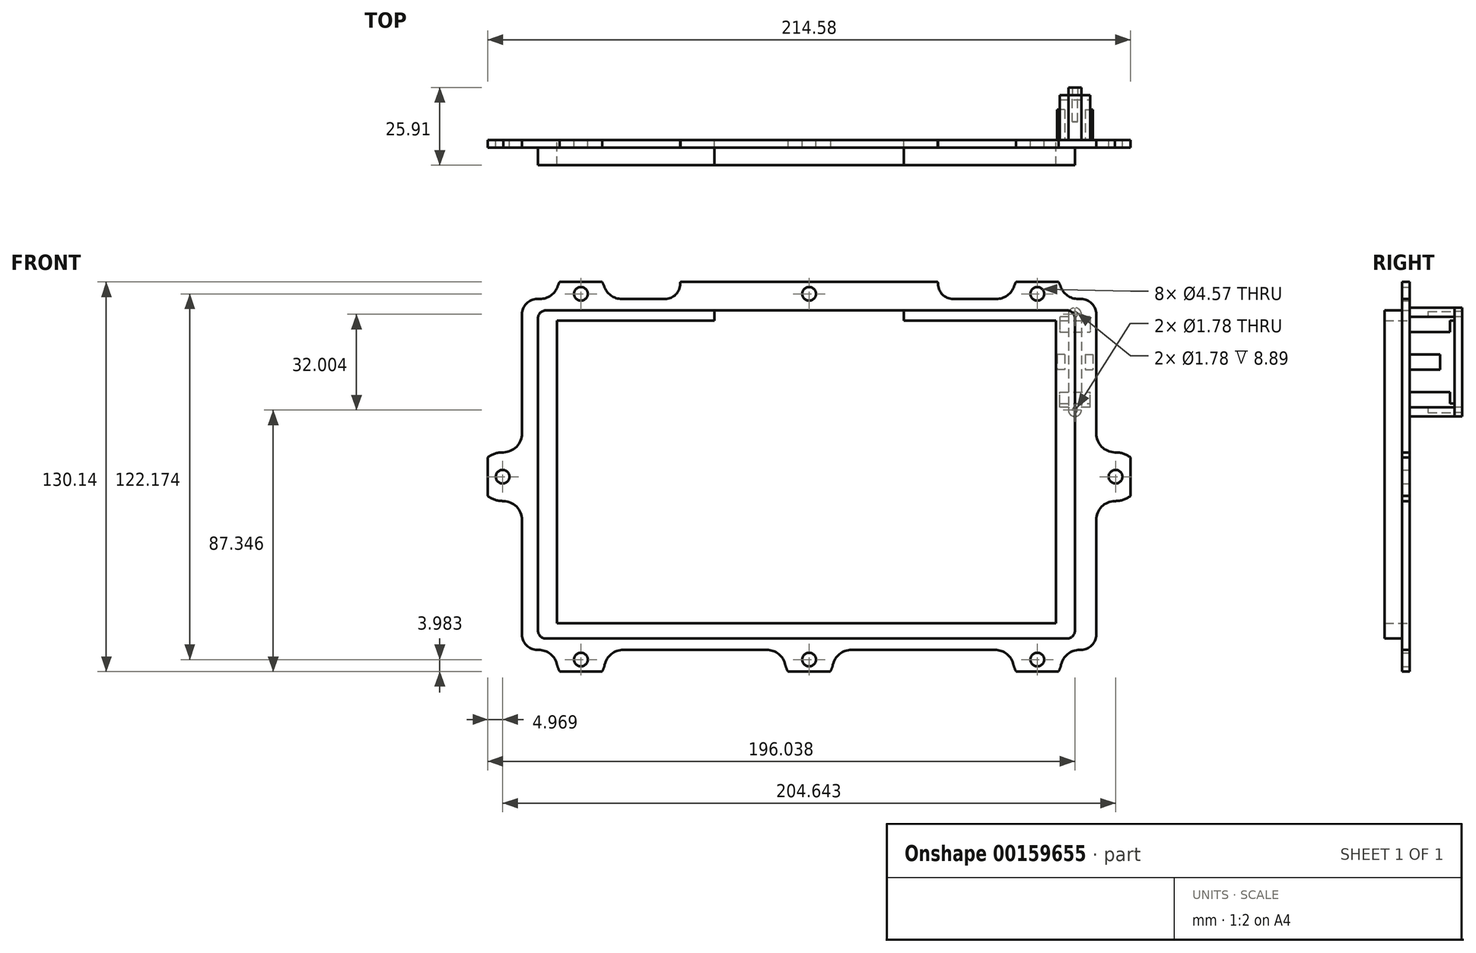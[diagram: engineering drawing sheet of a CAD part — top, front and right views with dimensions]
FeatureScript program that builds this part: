
annotation { "Feature Type Name" : "Feature", "Feature Type Description" : "" }
export const myFeature = defineFeature(function(context is Context, id is Id, definition is map)
    precondition{}
    {
        {
            var Q0;
            Q0=qCreatedBy(makeId("Front.planeOp"),FACE);
            var sketch = newSketch(context, id + "F0", { "sketchPlane" : qUnion([Q0])});
            skLineSegment(sketch, "E0.bottom", {"start": v(122.56, 76.2) * mm, "end": v(-122.56, 76.2) * mm});
            skLineSegment(sketch, "E0.top", {"start": v(122.55, -76.2) * mm, "end": v(-122.55, -76.2) * mm});
            skLineSegment(sketch, "E0.left", {"start": v(122.55, 76.2) * mm, "end": v(122.56, -76.2) * mm});
            skLineSegment(sketch, "E0.right", {"start": v(-122.56, 76.2) * mm, "end": v(-122.55, -76.2) * mm});
            skPoint(sketch, "E0.middle", {"position": v(0, 0) * mm});
            skLineSegment(sketch, "E1.bottom", {"start": v(-84.15, -48.95) * mm, "end": v(82.4, -48.95) * mm});
            skLineSegment(sketch, "E1.top", {"start": v(-84.15, 52.12) * mm, "end": v(-31.6, 52.12) * mm});
            skLineSegment(sketch, "E1.left", {"start": v(-84.15, -48.95) * mm, "end": v(-84.15, 52.12) * mm});
            skLineSegment(sketch, "E1.right", {"start": v(82.4, -48.95) * mm, "end": v(82.4, 52.12) * mm});
            skLineSegment(sketch, "E2", {"start": v(0, 76.2) * mm, "end": v(0, -76.2) * mm, "construction": true});
            skCircle(sketch, "E3", {"center": v(0, -61.09) * mm, "radius": 2.29 * mm});
            skCircle(sketch, "E4.MirrorC", {"center": v(0, 61.09) * mm, "radius": 2.29 * mm});
            skLineSegment(sketch, "E5.top", {"start": v(31.6, 55.55) * mm, "end": v(-31.6, 55.55) * mm});
            skLineSegment(sketch, "E5.left", {"start": v(31.6, 55.55) * mm, "end": v(31.6, 52.12) * mm});
            skLineSegment(sketch, "E5.right", {"start": v(-31.6, 55.55) * mm, "end": v(-31.6, 52.12) * mm});
            skLineSegment(sketch, "E6.trimOffspring", {"start": v(31.6, 52.12) * mm, "end": v(82.4, 52.12) * mm});
            skPoint(sketch, "E7.centerSnap0", {"position": v(-84.15, 1.59) * mm});
            skCircle(sketch, "E8", {"center": v(-102.32, 0) * mm, "radius": 2.29 * mm});
            skPoint(sketch, "E8.centerSnap0", {"position": v(-122.55, 0) * mm});
            skCircle(sketch, "E9.MirrorC", {"center": v(102.32, 0) * mm, "radius": 2.29 * mm});
            skCircle(sketch, "E10", {"center": v(-76.2, 61.09) * mm, "radius": 2.29 * mm});
            skCircle(sketch, "E11.MirrorC", {"center": v(76.2, 61.09) * mm, "radius": 2.29 * mm});
            skCircle(sketch, "E12.MirrorC", {"center": v(-76.2, -61.09) * mm, "radius": 2.29 * mm});
            skCircle(sketch, "E13.MirrorC", {"center": v(76.2, -61.09) * mm, "radius": 2.29 * mm});
            skSolve(sketch);
        }
        {
            var Q0;
            Q0 = qSketchRegion(id + "F0", true);
            extrude(context, id + "F1", {"entities" : qUnion([Q0]), "depth" : 2.54 * mm});
        }
        {
            var Q0;
            {var subQ0=sQuery(id+"F0.wireOp",EDGE,"E6.trimOffspring");var subQ1=sQuery(id+"F0.wireOp",EDGE,"E5.left");var subQ2=sQuery(id+"F0.wireOp",EDGE,"E1.bottom");var subQ3=sQuery(id+"F0.wireOp",EDGE,"E5.right");var subQ4=sQuery(id+"F0.wireOp",EDGE,"E0.right");var subQ5=sQuery(id+"F0.wireOp",EDGE,"E0.left");var subQ6=sQuery(id+"F0.wireOp",EDGE,"E0.bottom");var subQ7=sQuery(id+"F0.wireOp",EDGE,"E1.top");var subQ8=sQuery(id+"F0.wireOp",EDGE,"E1.left");var subQ9=sQuery(id+"F0.wireOp",EDGE,"E5.top");var subQ10=sQuery(id+"F0.wireOp",EDGE,"E1.right");Q0=makeQuery(id+"FoEDC6IaHk2UjBE_1.boolean.opBoolean","SPLIT",FACE,{"disambiguationData":[TD([makeQuery(id+"F1.opExtrude","SWEPT_FACE",FACE,{"disambiguationData":[OSD([subQ6])]})])],"derivedFrom":makeQuery(id+"F1.opExtrude","CAP_FACE",FACE,{"disambiguationData":[OSD([subQ6,sQuery(id+"F0.wireOp",EDGE,"E0.top"),subQ5,subQ4,subQ2,subQ7,subQ8,subQ10,sQuery(id+"F0.wireOp",EDGE,"E3"),sQuery(id+"F0.wireOp",EDGE,"sFVqbhVj-slte-m2BO-i9PR-RLCebhDjpQio"),sQuery(id+"F0.wireOp",EDGE,"nxVHSm6B-fOxF-N3zU-KlmY-iFDlvtlfsas0"),sQuery(id+"F0.wireOp",EDGE,"0cddea9b-7ac9-488d-9e64-17cf55ce85570.MirrorC"),sQuery(id+"F0.wireOp",EDGE,"E4.MirrorC"),sQuery(id+"F0.wireOp",EDGE,"3127313a-c26d-4710-95f3-0c9ef9dcd8090.MirrorC"),subQ9,subQ1,subQ3,subQ0])],"isStart":false})});}
            var sketch = newSketch(context, id + "F2", { "sketchPlane" : qUnion([Q0])});
            skLineSegment(sketch, "E14.bottom", {"start": v(88.75, -54.03) * mm, "end": v(-90.5, -54.03) * mm});
            skLineSegment(sketch, "E14.top", {"start": v(88.75, 55.55) * mm, "end": v(31.6, 55.55) * mm});
            skLineSegment(sketch, "E14.left", {"start": v(88.75, -54.03) * mm, "end": v(88.75, 55.55) * mm});
            skLineSegment(sketch, "E14.right", {"start": v(-90.5, -54.03) * mm, "end": v(-90.5, 55.55) * mm});
            skLineSegment(sketch, "E15.bottom", {"start": v(-84.15, -48.95) * mm, "end": v(82.4, -48.95) * mm});
            skLineSegment(sketch, "E15.top", {"start": v(-84.15, 52.12) * mm, "end": v(-31.6, 52.12) * mm});
            skLineSegment(sketch, "E15.left", {"start": v(-84.15, -48.95) * mm, "end": v(-84.15, 52.12) * mm});
            skLineSegment(sketch, "E15.right", {"start": v(82.4, -48.95) * mm, "end": v(82.4, 52.12) * mm});
            skLineSegment(sketch, "E16", {"start": v(31.6, 52.12) * mm, "end": v(31.6, 55.55) * mm});
            skLineSegment(sketch, "E17", {"start": v(-31.6, 52.12) * mm, "end": v(-31.6, 55.55) * mm});
            skLineSegment(sketch, "E18.trimOffspring", {"start": v(-31.6, 55.55) * mm, "end": v(-90.5, 55.55) * mm});
            skLineSegment(sketch, "E19.trimOffspring", {"start": v(31.6, 52.12) * mm, "end": v(82.4, 52.12) * mm});
            skSolve(sketch);
        }
        {
            var Q0;
            Q0 = qSketchRegion(id + "F2", true);
            extrude(context, id + "F3", {"entities" : qUnion([Q0]), "operationType" : NewBodyOperationType.ADD, "depth" : 5.84 * mm});
        }
        {
            var Q0;
            Q0=makeQuery(id+"F1.opExtrude","CAP_FACE",FACE,{"disambiguationData":[OSD([sQuery(id+"F0.wireOp",EDGE,"E0.bottom"),sQuery(id+"F0.wireOp",EDGE,"E0.top"),sQuery(id+"F0.wireOp",EDGE,"E0.left"),sQuery(id+"F0.wireOp",EDGE,"E0.right"),sQuery(id+"F0.wireOp",EDGE,"E1.bottom"),sQuery(id+"F0.wireOp",EDGE,"E1.top"),sQuery(id+"F0.wireOp",EDGE,"E1.left"),sQuery(id+"F0.wireOp",EDGE,"E1.right"),sQuery(id+"F0.wireOp",EDGE,"E3"),sQuery(id+"F0.wireOp",EDGE,"sFVqbhVj-slte-m2BO-i9PR-RLCebhDjpQio"),sQuery(id+"F0.wireOp",EDGE,"nxVHSm6B-fOxF-N3zU-KlmY-iFDlvtlfsas0"),sQuery(id+"F0.wireOp",EDGE,"0cddea9b-7ac9-488d-9e64-17cf55ce85570.MirrorC"),sQuery(id+"F0.wireOp",EDGE,"E4.MirrorC"),sQuery(id+"F0.wireOp",EDGE,"3127313a-c26d-4710-95f3-0c9ef9dcd8090.MirrorC"),sQuery(id+"F0.wireOp",EDGE,"E5.top"),sQuery(id+"F0.wireOp",EDGE,"E5.left"),sQuery(id+"F0.wireOp",EDGE,"E5.right"),sQuery(id+"F0.wireOp",EDGE,"E6.trimOffspring"),sQuery(id+"F0.wireOp",EDGE,"E8"),sQuery(id+"F0.wireOp",EDGE,"E9.MirrorC")])],"isStart":false});
            var sketch = newSketch(context, id + "F4", { "sketchPlane" : qUnion([Q0])});
            skLineSegment(sketch, "E20.bottom", {"start": v(-90.78, 59.36) * mm, "end": v(-89.92, 59.36) * mm});
            skLineSegment(sketch, "E20.top", {"start": v(-90.78, -57.84) * mm, "end": v(-90.34, -57.84) * mm});
            skLineSegment(sketch, "E20.left", {"start": v(-95.86, 54.28) * mm, "end": v(-95.86, 14.48) * mm});
            skLineSegment(sketch, "E20.right", {"start": v(95.86, 54.28) * mm, "end": v(95.86, 14.48) * mm});
            skArc(sketch, "E21.MirrorC", {"start": v(7.94, -62.83) * mm, "mid": v(0, -69.21) * mm, "end": v(-7.94, -62.83) * mm});
            skArc(sketch, "E22.0", {"start": v(-102.32, 8.13) * mm, "mid": v(-110.45, 0) * mm, "end": v(-102.32, -8.13) * mm});
            skArc(sketch, "E23.MirrorC", {"start": v(102.32, 8.13) * mm, "mid": v(110.45, 0) * mm, "end": v(102.32, -8.13) * mm});
            skLineSegment(sketch, "E24", {"start": v(-102.32, 8.13) * mm, "end": v(-102.14, 8.13) * mm});
            skLineSegment(sketch, "E25", {"start": v(-102.32, -8.13) * mm, "end": v(-102.14, -8.13) * mm});
            skLineSegment(sketch, "E26.MirrorCS", {"start": v(102.32, 8.13) * mm, "end": v(102.14, 8.13) * mm});
            skLineSegment(sketch, "E27.MirrorCS", {"start": v(102.32, -8.13) * mm, "end": v(102.14, -8.13) * mm});
            skLineSegment(sketch, "E28.trimOffspring", {"start": v(-62.48, 59.36) * mm, "end": v(-48.1, 59.36) * mm});
            skLineSegment(sketch, "E29.trimOffspring", {"start": v(48.1, 59.36) * mm, "end": v(62.48, 59.36) * mm});
            skLineSegment(sketch, "E30.trimOffspring", {"start": v(89.92, 59.36) * mm, "end": v(90.78, 59.36) * mm});
            skLineSegment(sketch, "E31.trimOffspring", {"start": v(95.86, -14.48) * mm, "end": v(95.86, -52.76) * mm});
            skLineSegment(sketch, "E32.trimOffspring", {"start": v(90.34, -57.84) * mm, "end": v(90.78, -57.84) * mm});
            skLineSegment(sketch, "E33.trimOffspring", {"start": v(14.14, -57.84) * mm, "end": v(62.06, -57.84) * mm});
            skLineSegment(sketch, "E34.trimOffspring", {"start": v(-62.06, -57.84) * mm, "end": v(-14.14, -57.84) * mm});
            skLineSegment(sketch, "E35.trimOffspring", {"start": v(-95.86, -14.48) * mm, "end": v(-95.86, -52.76) * mm});
            skLineSegment(sketch, "E36.bottom", {"start": v(-122.56, 76.2) * mm, "end": v(122.56, 76.2) * mm});
            skLineSegment(sketch, "E36.top", {"start": v(-122.56, -76.2) * mm, "end": v(122.56, -76.2) * mm});
            skLineSegment(sketch, "E36.left", {"start": v(-122.56, 76.2) * mm, "end": v(-122.56, -76.2) * mm});
            skLineSegment(sketch, "E36.right", {"start": v(122.56, 76.2) * mm, "end": v(122.56, -76.2) * mm});
            skLineSegment(sketch, "E37", {"start": v(43.03, 64.44) * mm, "end": v(43.03, 64.44) * mm});
            skLineSegment(sketch, "E38", {"start": v(40.49, 66.98) * mm, "end": v(8.65, 66.98) * mm});
            skLineSegment(sketch, "E39", {"start": v(-43.03, 64.44) * mm, "end": v(-43.03, 64.44) * mm});
            skPoint(sketch, "E40.MirrorCS.end.orphan", {"position": v(6.92, 59.36) * mm});
            skPoint(sketch, "E41.orphan", {"position": v(8.13, 61.09) * mm});
            skPoint(sketch, "E42.orphan", {"position": v(-6.92, 59.36) * mm});
            skPoint(sketch, "E43.orphan", {"position": v(-8.13, 61.09) * mm});
            skPoint(sketch, "E44.visualSharp", {"position": v(43.03, 59.36) * mm});
            skArc(sketch, "E44.filletArc", {"start": v(43.03, 64.44) * mm, "mid": v(44.52, 60.85) * mm, "end": v(48.1, 59.36) * mm});
            skPoint(sketch, "E45.visualSharp", {"position": v(-43.03, 59.36) * mm});
            skArc(sketch, "E45.filletArc", {"start": v(-48.1, 59.36) * mm, "mid": v(-44.52, 60.85) * mm, "end": v(-43.03, 64.44) * mm});
            skPoint(sketch, "E46.visualSharp", {"position": v(95.86, 59.36) * mm});
            skArc(sketch, "E46.filletArc", {"start": v(95.86, 54.28) * mm, "mid": v(94.37, 57.87) * mm, "end": v(90.78, 59.36) * mm});
            skPoint(sketch, "E47.visualSharp", {"position": v(95.86, -57.84) * mm});
            skArc(sketch, "E47.filletArc", {"start": v(90.78, -57.84) * mm, "mid": v(94.37, -56.35) * mm, "end": v(95.86, -52.76) * mm});
            skPoint(sketch, "E48.visualSharp", {"position": v(-95.86, -57.84) * mm});
            skArc(sketch, "E48.filletArc", {"start": v(-95.86, -52.76) * mm, "mid": v(-94.37, -56.35) * mm, "end": v(-90.78, -57.84) * mm});
            skPoint(sketch, "E49.visualSharp", {"position": v(-95.86, 59.36) * mm});
            skArc(sketch, "E49.filletArc", {"start": v(-90.78, 59.36) * mm, "mid": v(-94.37, 57.87) * mm, "end": v(-95.86, 54.28) * mm});
            skLineSegment(sketch, "E50.trimOffspring", {"start": v(8.65, 66.98) * mm, "end": v(-40.49, 66.98) * mm});
            skPoint(sketch, "E51.orphan", {"position": v(-6.92, -59.36) * mm});
            skPoint(sketch, "E52.orphan", {"position": v(6.92, -59.36) * mm});
            skPoint(sketch, "E53.orphan", {"position": v(-83.25, 59.36) * mm});
            skPoint(sketch, "E54.orphan", {"position": v(83.25, 59.36) * mm});
            skArc(sketch, "E55.0", {"start": v(-68.5, 63.68) * mm, "mid": v(-76.2, 69.22) * mm, "end": v(-83.9, 63.68) * mm});
            skArc(sketch, "E56.MirrorC", {"start": v(-68.26, -62.83) * mm, "mid": v(-76.2, -69.22) * mm, "end": v(-84.14, -62.83) * mm});
            skArc(sketch, "E57.MirrorC", {"start": v(68.26, -62.83) * mm, "mid": v(76.2, -69.22) * mm, "end": v(84.14, -62.83) * mm});
            skArc(sketch, "E58.MirrorC", {"start": v(68.5, 63.68) * mm, "mid": v(76.2, 69.22) * mm, "end": v(83.9, 63.68) * mm});
            skPoint(sketch, "E59.visualSharp", {"position": v(-43.03, 66.98) * mm});
            skArc(sketch, "E59.filletArc", {"start": v(-40.49, 66.98) * mm, "mid": v(-42.28, 66.24) * mm, "end": v(-43.03, 64.44) * mm});
            skPoint(sketch, "E60.visualSharp", {"position": v(43.03, 66.98) * mm});
            skArc(sketch, "E60.filletArc", {"start": v(43.03, 64.44) * mm, "mid": v(42.28, 66.24) * mm, "end": v(40.49, 66.98) * mm});
            skPoint(sketch, "E61.newPointA", {"position": v(-83.12, 59.86) * mm});
            skPoint(sketch, "E62.newPointA", {"position": v(-69.15, 59.36) * mm});
            skPoint(sketch, "E62.newPointB", {"position": v(-69.28, 59.86) * mm});
            skPoint(sketch, "E63.visualSharp", {"position": v(-95.86, 8.13) * mm});
            skPoint(sketch, "E64.visualSharp", {"position": v(-95.86, -8.13) * mm});
            skPoint(sketch, "E65.newPointB", {"position": v(-83.12, -59.86) * mm});
            skPoint(sketch, "E66.newPointA", {"position": v(-69.28, -59.86) * mm});
            skPoint(sketch, "E67.visualSharp", {"position": v(-6.92, -57.84) * mm});
            skPoint(sketch, "E68.visualSharp", {"position": v(6.92, -57.84) * mm});
            skPoint(sketch, "E69.newPointA", {"position": v(69.28, -59.86) * mm});
            skPoint(sketch, "E70.newPointA", {"position": v(83.12, -59.86) * mm});
            skPoint(sketch, "E71.visualSharp", {"position": v(95.86, -8.13) * mm});
            skPoint(sketch, "E72.visualSharp", {"position": v(95.86, 8.13) * mm});
            skPoint(sketch, "E73.newPointA", {"position": v(83.12, 59.86) * mm});
            skPoint(sketch, "E74.newPointA", {"position": v(69.28, 59.86) * mm});
            skPoint(sketch, "E74.newPointB", {"position": v(69.15, 59.36) * mm});
            skArc(sketch, "E75", {"start": v(-68.5, 63.68) * mm, "mid": v(-66.18, 60.55) * mm, "end": v(-62.48, 59.36) * mm});
            skArc(sketch, "E76", {"start": v(-89.92, 59.36) * mm, "mid": v(-86.22, 60.55) * mm, "end": v(-83.9, 63.68) * mm});
            skArc(sketch, "E77", {"start": v(-102.28, 8.13) * mm, "mid": v(-97.75, 9.96) * mm, "end": v(-95.86, 14.48) * mm});
            skArc(sketch, "E78", {"start": v(-7.94, -62.83) * mm, "mid": v(-10.16, -59.24) * mm, "end": v(-14.14, -57.84) * mm});
            skArc(sketch, "E79", {"start": v(-95.86, -14.48) * mm, "mid": v(-97.75, -9.96) * mm, "end": v(-102.28, -8.13) * mm});
            skArc(sketch, "E80", {"start": v(-84.14, -62.83) * mm, "mid": v(-86.36, -59.24) * mm, "end": v(-90.34, -57.84) * mm});
            skArc(sketch, "E81", {"start": v(-62.06, -57.84) * mm, "mid": v(-66.04, -59.24) * mm, "end": v(-68.26, -62.83) * mm});
            skArc(sketch, "E82", {"start": v(14.14, -57.84) * mm, "mid": v(10.16, -59.24) * mm, "end": v(7.94, -62.83) * mm});
            skArc(sketch, "E83", {"start": v(68.26, -62.83) * mm, "mid": v(66.04, -59.24) * mm, "end": v(62.06, -57.84) * mm});
            skArc(sketch, "E84", {"start": v(90.34, -57.84) * mm, "mid": v(86.36, -59.24) * mm, "end": v(84.14, -62.83) * mm});
            skArc(sketch, "E85", {"start": v(102.28, -8.13) * mm, "mid": v(97.75, -9.96) * mm, "end": v(95.86, -14.48) * mm});
            skArc(sketch, "E86", {"start": v(95.86, 14.48) * mm, "mid": v(97.75, 9.96) * mm, "end": v(102.28, 8.13) * mm});
            skArc(sketch, "E87", {"start": v(62.48, 59.36) * mm, "mid": v(66.18, 60.55) * mm, "end": v(68.5, 63.68) * mm});
            skArc(sketch, "E88", {"start": v(83.9, 63.68) * mm, "mid": v(86.22, 60.55) * mm, "end": v(89.92, 59.36) * mm});
            skPoint(sketch, "E89.start.orphan", {"position": v(-84.33, 61.09) * mm});
            skPoint(sketch, "E90.start.orphan", {"position": v(-68.07, 61.09) * mm});
            skPoint(sketch, "E91.orphan", {"position": v(-84.33, -61.09) * mm});
            skPoint(sketch, "E92.MirrorCS.start.orphan", {"position": v(-68.07, -61.09) * mm});
            skPoint(sketch, "E93.orphan", {"position": v(-8.13, -61.09) * mm});
            skPoint(sketch, "E94.orphan", {"position": v(8.13, -61.09) * mm});
            skPoint(sketch, "E95.orphan", {"position": v(68.07, -61.09) * mm});
            skPoint(sketch, "E96.orphan", {"position": v(84.33, -61.09) * mm});
            skPoint(sketch, "E97.MirrorCS.start.orphan", {"position": v(84.33, 61.09) * mm});
            skPoint(sketch, "E98.MirrorCS.start.orphan", {"position": v(68.07, 61.09) * mm});
            skSolve(sketch);
        }
        {
            var Q0;
            Q0 = qSketchRegion(id + "F4", true);
            extrude(context, id + "F5", {"entities" : qUnion([Q0]), "operationType" : NewBodyOperationType.REMOVE, "oppositeDirection" : true, "depth" : 25.4 * mm});
        }
        {
            var Q0;
            Q0=makeQuery(id+"F3.opExtrude","SWEPT_EDGE",EDGE,{"disambiguationData":[OSD([sQuery(id+"F2.wireOp",EDGE,"E14.right"),sQuery(id+"F2.wireOp",EDGE,"E18.trimOffspring")])]});
            var Q1;
            Q1=makeQuery(id+"F3.opExtrude","SWEPT_EDGE",EDGE,{"disambiguationData":[OSD([sQuery(id+"F2.wireOp",EDGE,"E14.bottom"),sQuery(id+"F2.wireOp",EDGE,"E14.right")])]});
            var Q2;
            Q2=makeQuery(id+"F3.opExtrude","SWEPT_EDGE",EDGE,{"disambiguationData":[OSD([sQuery(id+"F2.wireOp",EDGE,"E14.top"),sQuery(id+"F2.wireOp",EDGE,"E14.left")])]});
            var Q3;
            Q3=makeQuery(id+"F3.opExtrude","SWEPT_EDGE",EDGE,{"disambiguationData":[OSD([sQuery(id+"F2.wireOp",EDGE,"E14.bottom"),sQuery(id+"F2.wireOp",EDGE,"E14.left")])]});
            fillet(context, id + "F6", {"entities" : qUnion([Q0, Q1, Q2, Q3]), "radius" : 2.54 * mm, "tangentPropagation" : true, "allowEdgeOverflow" : false});
        }
        {
            var Q0;
            Q0=qCreatedBy(makeId("Front.planeOp"),FACE);
            var sketch = newSketch(context, id + "F7", { "sketchPlane" : qUnion([Q0])});
            skLineSegment(sketch, "E99.bottom", {"start": v(107.29, 65.07) * mm, "end": v(-107.29, 65.07) * mm});
            skLineSegment(sketch, "E99.top", {"start": v(107.29, -65.07) * mm, "end": v(-107.29, -65.07) * mm});
            skLineSegment(sketch, "E99.left", {"start": v(107.29, 65.07) * mm, "end": v(107.29, -65.07) * mm});
            skLineSegment(sketch, "E99.right", {"start": v(-107.29, 65.07) * mm, "end": v(-107.29, -65.07) * mm});
            skPoint(sketch, "E99.middle", {"position": v(0, 0) * mm});
            skLineSegment(sketch, "E100.bottom", {"start": v(129.14, 87.93) * mm, "end": v(-129.14, 87.93) * mm});
            skLineSegment(sketch, "E100.top", {"start": v(129.14, -87.93) * mm, "end": v(-129.14, -87.93) * mm});
            skLineSegment(sketch, "E100.left", {"start": v(129.14, 87.93) * mm, "end": v(129.14, -87.93) * mm});
            skLineSegment(sketch, "E100.right", {"start": v(-129.14, 87.93) * mm, "end": v(-129.14, -87.93) * mm});
            skSolve(sketch);
        }
        {
            var Q0;
            Q0 = qSketchRegion(id + "F7", true);
            extrude(context, id + "F8", {"entities" : qUnion([Q0]), "operationType" : NewBodyOperationType.REMOVE, "endBound" : BoundingType.THROUGH_ALL, "depth" : 25.4 * mm});
        }
        {
            var Q0;
            Q0=makeQuery(id+"F1.opExtrude","CAP_FACE",FACE,{"disambiguationData":[OSD([sQuery(id+"F0.wireOp",EDGE,"E0.bottom"),sQuery(id+"F0.wireOp",EDGE,"E0.top"),sQuery(id+"F0.wireOp",EDGE,"E0.left"),sQuery(id+"F0.wireOp",EDGE,"E0.right"),sQuery(id+"F0.wireOp",EDGE,"E1.bottom"),sQuery(id+"F0.wireOp",EDGE,"E1.top"),sQuery(id+"F0.wireOp",EDGE,"E1.left"),sQuery(id+"F0.wireOp",EDGE,"E1.right"),sQuery(id+"F0.wireOp",EDGE,"E3"),sQuery(id+"F0.wireOp",EDGE,"E4.MirrorC"),sQuery(id+"F0.wireOp",EDGE,"E5.top"),sQuery(id+"F0.wireOp",EDGE,"E5.left"),sQuery(id+"F0.wireOp",EDGE,"E5.right"),sQuery(id+"F0.wireOp",EDGE,"E6.trimOffspring"),sQuery(id+"F0.wireOp",EDGE,"E8"),sQuery(id+"F0.wireOp",EDGE,"E9.MirrorC"),sQuery(id+"F0.wireOp",EDGE,"E10"),sQuery(id+"F0.wireOp",EDGE,"E11.MirrorC"),sQuery(id+"F0.wireOp",EDGE,"E12.MirrorC"),sQuery(id+"F0.wireOp",EDGE,"E13.MirrorC")])],"isStart":true});
            var sketch = newSketch(context, id + "F9", { "sketchPlane" : qUnion([Q0])});
            skLineSegment(sketch, "E101.bottom", {"start": v(-83.67, 52.12) * mm, "end": v(-93.83, 52.12) * mm});
            skLineSegment(sketch, "E101.top", {"start": v(-83.67, 48.31) * mm, "end": v(-93.83, 48.31) * mm});
            skLineSegment(sketch, "E101.left", {"start": v(-83.67, 52.12) * mm, "end": v(-83.67, 48.31) * mm});
            skLineSegment(sketch, "E101.right", {"start": v(-93.83, 52.12) * mm, "end": v(-93.83, 48.31) * mm});
            skLineSegment(sketch, "E102", {"start": v(-59.95, 38.28) * mm, "end": v(-132.53, 38.28) * mm, "construction": true});
            skLineSegment(sketch, "E103.MirrorCS", {"start": v(-83.67, 24.43) * mm, "end": v(-83.67, 28.24) * mm});
            skLineSegment(sketch, "E104.MirrorCS", {"start": v(-83.67, 24.43) * mm, "end": v(-93.83, 24.43) * mm});
            skLineSegment(sketch, "E105.MirrorCS", {"start": v(-93.83, 24.43) * mm, "end": v(-93.83, 28.24) * mm});
            skLineSegment(sketch, "E106.MirrorCS", {"start": v(-83.67, 28.24) * mm, "end": v(-93.83, 28.24) * mm});
            skSolve(sketch);
        }
        {
            var Q0;
            Q0 = qSketchRegion(id + "F9", true);
            extrude(context, id + "F10", {"entities" : qUnion([Q0]), "operationType" : NewBodyOperationType.ADD, "depth" : 13.46 * mm});
        }
        {
            var Q0;
            Q0=makeQuery(id+"F1.opExtrude","CAP_FACE",FACE,{"disambiguationData":[OSD([sQuery(id+"F0.wireOp",EDGE,"E0.bottom"),sQuery(id+"F0.wireOp",EDGE,"E0.top"),sQuery(id+"F0.wireOp",EDGE,"E0.left"),sQuery(id+"F0.wireOp",EDGE,"E0.right"),sQuery(id+"F0.wireOp",EDGE,"E1.bottom"),sQuery(id+"F0.wireOp",EDGE,"E1.top"),sQuery(id+"F0.wireOp",EDGE,"E1.left"),sQuery(id+"F0.wireOp",EDGE,"E1.right"),sQuery(id+"F0.wireOp",EDGE,"E3"),sQuery(id+"F0.wireOp",EDGE,"E4.MirrorC"),sQuery(id+"F0.wireOp",EDGE,"E5.top"),sQuery(id+"F0.wireOp",EDGE,"E5.left"),sQuery(id+"F0.wireOp",EDGE,"E5.right"),sQuery(id+"F0.wireOp",EDGE,"E6.trimOffspring"),sQuery(id+"F0.wireOp",EDGE,"E8"),sQuery(id+"F0.wireOp",EDGE,"E9.MirrorC"),sQuery(id+"F0.wireOp",EDGE,"E10"),sQuery(id+"F0.wireOp",EDGE,"E11.MirrorC"),sQuery(id+"F0.wireOp",EDGE,"E12.MirrorC"),sQuery(id+"F0.wireOp",EDGE,"E13.MirrorC")])],"isStart":true});
            var sketch = newSketch(context, id + "F11", { "sketchPlane" : qUnion([Q0])});
            skLineSegment(sketch, "E107.bottom", {"start": v(-93.83, 53.4) * mm, "end": v(-83.67, 53.4) * mm});
            skLineSegment(sketch, "E107.top", {"start": v(-93.83, 52.12) * mm, "end": v(-83.67, 52.12) * mm});
            skLineSegment(sketch, "E107.left", {"start": v(-93.83, 53.4) * mm, "end": v(-93.83, 52.12) * mm});
            skLineSegment(sketch, "E107.right", {"start": v(-83.67, 53.4) * mm, "end": v(-83.67, 52.12) * mm});
            skCircle(sketch, "E108", {"center": v(-88.75, 54.28) * mm, "radius": 2.16 * mm});
            skPoint(sketch, "E108.centerSnap0", {"position": v(-88.75, 53.4) * mm});
            skLineSegment(sketch, "E109", {"start": v(-58.46, 38.28) * mm, "end": v(-105.08, 38.28) * mm, "construction": true});
            skLineSegment(sketch, "E110.MirrorCS", {"start": v(-93.83, 24.43) * mm, "end": v(-83.67, 24.43) * mm});
            skLineSegment(sketch, "E111.MirrorCS", {"start": v(-83.67, 23.16) * mm, "end": v(-83.67, 24.43) * mm});
            skLineSegment(sketch, "E112.MirrorCS", {"start": v(-93.83, 23.16) * mm, "end": v(-83.67, 23.16) * mm});
            skLineSegment(sketch, "E113.MirrorCS", {"start": v(-93.83, 23.16) * mm, "end": v(-93.83, 24.43) * mm});
            skCircle(sketch, "E114.MirrorC", {"center": v(-88.75, 22.28) * mm, "radius": 2.16 * mm});
            skSolve(sketch);
        }
        {
            var Q0;
            Q0 = qSketchRegion(id + "F11", true);
            extrude(context, id + "F12", {"entities" : qUnion([Q0]), "operationType" : NewBodyOperationType.ADD, "depth" : 15 * mm});
        }
        {
            var Q0;
            Q0=makeQuery(id+"F12.opExtrude","CAP_FACE",FACE,{"disambiguationData":[OSD([sQuery(id+"F11.wireOp",EDGE,"E107.bottom"),sQuery(id+"F11.wireOp",EDGE,"E107.top"),sQuery(id+"F11.wireOp",EDGE,"E107.left"),sQuery(id+"F11.wireOp",EDGE,"E107.right"),sQuery(id+"F11.wireOp",EDGE,"E108")])],"isStart":false});
            var sketch = newSketch(context, id + "F13", { "sketchPlane" : qUnion([Q0])});
            skCircle(sketch, "E115", {"center": v(-88.75, 54.28) * mm, "radius": 0.89 * mm});
            skCircle(sketch, "E116", {"center": v(-88.75, 22.28) * mm, "radius": 0.89 * mm});
            skSolve(sketch);
        }
        {
            var Q0;
            Q0 = qSketchRegion(id + "F13", true);
            extrude(context, id + "F14", {"entities" : qUnion([Q0]), "operationType" : NewBodyOperationType.REMOVE, "oppositeDirection" : true, "depth" : 8.9 * mm});
        }
        {
            var Q0;
            Q0=makeQuery(id+"F12.opExtrude","CAP_FACE",FACE,{"disambiguationData":[OSD([sQuery(id+"F11.wireOp",EDGE,"E107.bottom"),sQuery(id+"F11.wireOp",EDGE,"E107.top"),sQuery(id+"F11.wireOp",EDGE,"E107.left"),sQuery(id+"F11.wireOp",EDGE,"E107.right"),sQuery(id+"F11.wireOp",EDGE,"E108")])],"isStart":false});
            var sketch = newSketch(context, id + "F15", { "sketchPlane" : qUnion([Q0])});
            skArc(sketch, "E117.0", {"start": v(-86.59, 54.28) * mm, "mid": v(-88.75, 56.44) * mm, "end": v(-90.9, 54.28) * mm});
            skArc(sketch, "E118.0", {"start": v(-86.59, 22.28) * mm, "mid": v(-88.75, 20.12) * mm, "end": v(-90.9, 22.28) * mm});
            skLineSegment(sketch, "E119", {"start": v(-86.59, 54.28) * mm, "end": v(-86.59, 22.28) * mm});
            skLineSegment(sketch, "E120", {"start": v(-90.9, 54.28) * mm, "end": v(-90.9, 22.28) * mm});
            skPoint(sketch, "E121.orphan", {"position": v(-86.78, 23.16) * mm});
            skPoint(sketch, "E122.orphan", {"position": v(-90.72, 23.16) * mm});
            skPoint(sketch, "E123.orphan", {"position": v(-86.78, 53.4) * mm});
            skPoint(sketch, "E124.orphan", {"position": v(-90.72, 53.4) * mm});
            skCircle(sketch, "E125.0", {"center": v(-88.75, 54.28) * mm, "radius": 0.89 * mm});
            skCircle(sketch, "E126.0", {"center": v(-88.75, 22.28) * mm, "radius": 0.89 * mm});
            skSolve(sketch);
        }
        {
            var Q0;
            Q0 = qSketchRegion(id + "F15", true);
            extrude(context, id + "F16", {"entities" : qUnion([Q0]), "depth" : 2.54 * mm});
        }
        {
            var Q0;
            Q0=makeQuery(id+"F1.opExtrude","CAP_FACE",FACE,{"disambiguationData":[OSD([sQuery(id+"F0.wireOp",EDGE,"E0.bottom"),sQuery(id+"F0.wireOp",EDGE,"E0.top"),sQuery(id+"F0.wireOp",EDGE,"E0.left"),sQuery(id+"F0.wireOp",EDGE,"E0.right"),sQuery(id+"F0.wireOp",EDGE,"E1.bottom"),sQuery(id+"F0.wireOp",EDGE,"E1.top"),sQuery(id+"F0.wireOp",EDGE,"E1.left"),sQuery(id+"F0.wireOp",EDGE,"E1.right"),sQuery(id+"F0.wireOp",EDGE,"E3"),sQuery(id+"F0.wireOp",EDGE,"E4.MirrorC"),sQuery(id+"F0.wireOp",EDGE,"E5.top"),sQuery(id+"F0.wireOp",EDGE,"E5.left"),sQuery(id+"F0.wireOp",EDGE,"E5.right"),sQuery(id+"F0.wireOp",EDGE,"E6.trimOffspring"),sQuery(id+"F0.wireOp",EDGE,"E8"),sQuery(id+"F0.wireOp",EDGE,"E9.MirrorC"),sQuery(id+"F0.wireOp",EDGE,"E10"),sQuery(id+"F0.wireOp",EDGE,"E11.MirrorC"),sQuery(id+"F0.wireOp",EDGE,"E12.MirrorC"),sQuery(id+"F0.wireOp",EDGE,"E13.MirrorC")])],"isStart":true});
            var sketch = newSketch(context, id + "F17", { "sketchPlane" : qUnion([Q0])});
            skLineSegment(sketch, "E127", {"start": v(-88.75, 48.31) * mm, "end": v(-88.75, 28.24) * mm, "construction": true});
            skLineSegment(sketch, "E128.bottom", {"start": v(-92.18, 40.82) * mm, "end": v(-94.72, 40.82) * mm});
            skLineSegment(sketch, "E128.top", {"start": v(-92.18, 35.74) * mm, "end": v(-94.72, 35.74) * mm});
            skLineSegment(sketch, "E128.left", {"start": v(-92.18, 40.82) * mm, "end": v(-92.18, 35.74) * mm});
            skLineSegment(sketch, "E128.right", {"start": v(-94.72, 40.82) * mm, "end": v(-94.72, 35.74) * mm});
            skLineSegment(sketch, "E129", {"start": v(-88.75, 38.28) * mm, "end": v(-74.88, 38.28) * mm, "construction": true});
            skPoint(sketch, "E129.endSnap0", {"position": v(-88.75, 38.28) * mm});
            skLineSegment(sketch, "E130.MirrorCS", {"start": v(-85.32, 40.82) * mm, "end": v(-82.78, 40.82) * mm});
            skLineSegment(sketch, "E131.MirrorCS", {"start": v(-82.78, 40.82) * mm, "end": v(-82.78, 35.74) * mm});
            skLineSegment(sketch, "E132.MirrorCS", {"start": v(-85.32, 35.74) * mm, "end": v(-82.78, 35.74) * mm});
            skLineSegment(sketch, "E133.MirrorCS", {"start": v(-85.32, 40.82) * mm, "end": v(-85.32, 35.74) * mm});
            skSolve(sketch);
        }
        {
            var Q0;
            Q0 = qSketchRegion(id + "F17", true);
            extrude(context, id + "F18", {"entities" : qUnion([Q0]), "operationType" : NewBodyOperationType.ADD, "depth" : 10.16 * mm});
        }
    });
